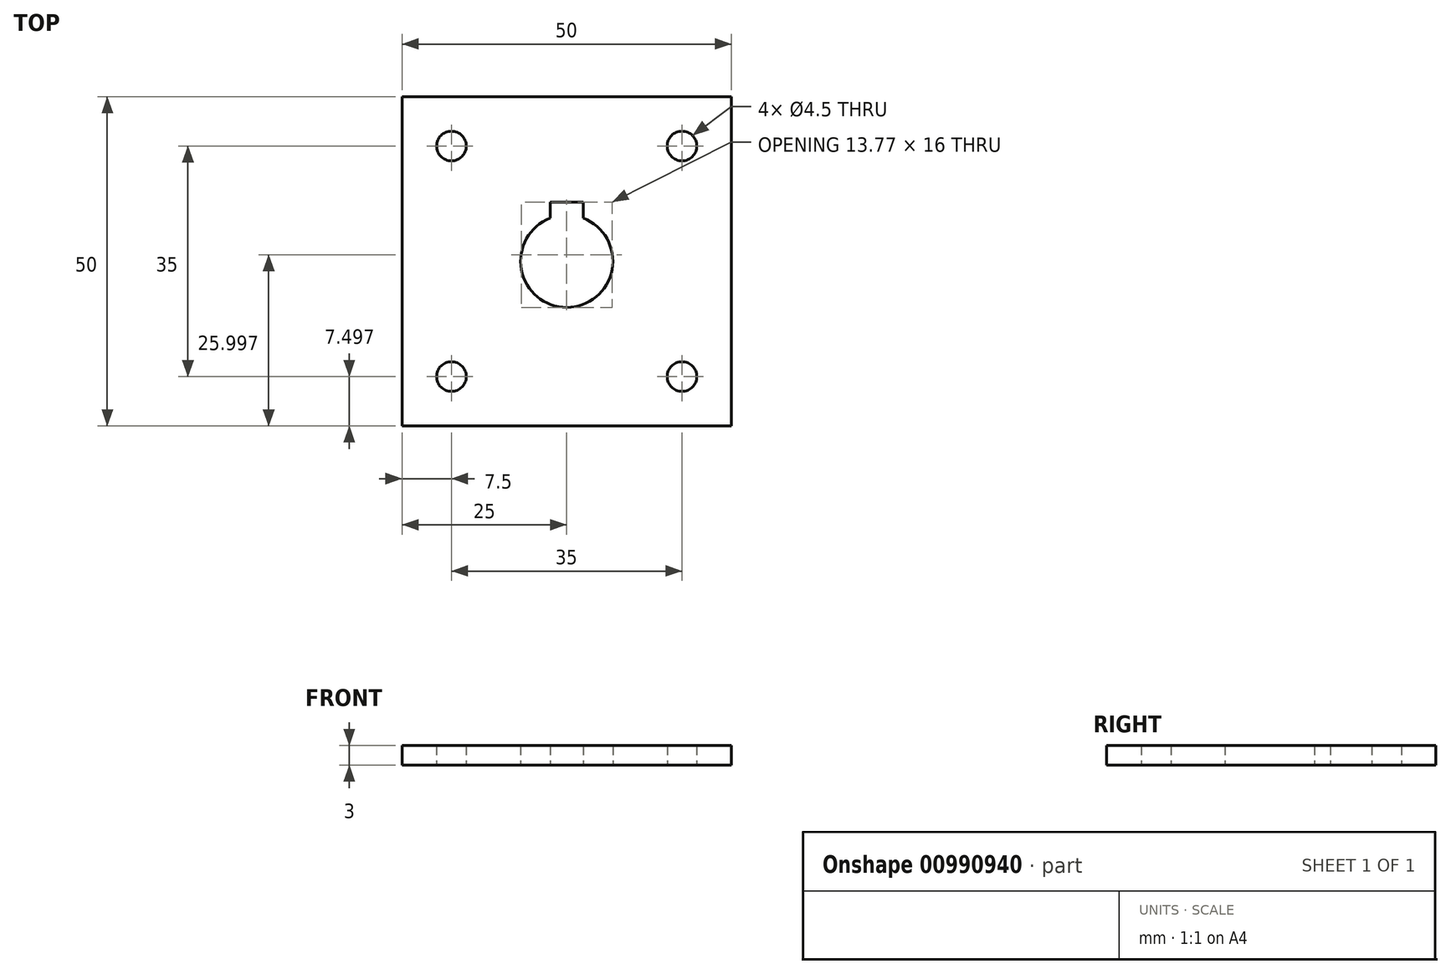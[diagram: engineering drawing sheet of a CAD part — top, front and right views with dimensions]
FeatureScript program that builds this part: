
annotation { "Feature Type Name" : "Feature", "Feature Type Description" : "" }
export const myFeature = defineFeature(function(context is Context, id is Id, definition is map)
    precondition{}
    {
        {
            var Q0;
            Q0=qCreatedBy(makeId("Top.planeOp"),FACE);
            var sketch = newSketch(context, id + "F0", { "sketchPlane" : qUnion([Q0])});
            skLineSegment(sketch, "E0.bottom", {"start": v(-75, -24.97) * mm, "end": v(-25, -24.97) * mm});
            skLineSegment(sketch, "E0.top", {"start": v(-75, -74.97) * mm, "end": v(-25, -74.97) * mm});
            skLineSegment(sketch, "E0.left", {"start": v(-75, -24.97) * mm, "end": v(-75, -74.97) * mm});
            skLineSegment(sketch, "E0.right", {"start": v(-25, -24.97) * mm, "end": v(-25, -74.97) * mm});
            skLineSegment(sketch, "E1", {"start": v(-25, -67.47) * mm, "end": v(-75, -67.47) * mm, "construction": true});
            skLineSegment(sketch, "E2", {"start": v(-25, -32.47) * mm, "end": v(-75, -32.47) * mm, "construction": true});
            skLineSegment(sketch, "E3", {"start": v(-32.5, -24.97) * mm, "end": v(-32.5, -74.97) * mm, "construction": true});
            skLineSegment(sketch, "E4", {"start": v(-67.5, -74.97) * mm, "end": v(-67.5, -24.97) * mm, "construction": true});
            skLineSegment(sketch, "E5", {"start": v(-50, -74.97) * mm, "end": v(-50, -24.97) * mm, "construction": true});
            skLineSegment(sketch, "E6", {"start": v(-47.5, -43.43) * mm, "end": v(-47.5, -40.97) * mm});
            skLineSegment(sketch, "E7", {"start": v(-47.5, -40.97) * mm, "end": v(-52.5, -40.97) * mm});
            skLineSegment(sketch, "E8", {"start": v(-52.5, -40.97) * mm, "end": v(-52.5, -43.43) * mm});
            skCircle(sketch, "E9", {"center": v(-32.5, -67.47) * mm, "radius": 2 * mm});
            skCircle(sketch, "E10", {"center": v(-67.5, -67.47) * mm, "radius": 2 * mm});
            skCircle(sketch, "E11", {"center": v(-32.5, -32.47) * mm, "radius": 2 * mm});
            skCircle(sketch, "E12", {"center": v(-67.5, -32.47) * mm, "radius": 2 * mm});
            skLineSegment(sketch, "E13", {"start": v(-25, -49.97) * mm, "end": v(-75, -49.97) * mm, "construction": true});
            skCircle(sketch, "E14.converted", {"center": v(-50, -49.97) * mm, "radius": 7 * mm});
            skSolve(sketch);
        }
        {
            var Q0;
            Q0=makeQuery(id+"F0.imprint","IMPRINT",FACE,{"disambiguationData":[TD([[makeQuery(id+"F0.imprint","IMPRINT",EDGE,{"derivedFrom":sQuery(id+"F0.wireOp",EDGE,"E0.bottom")}),-1.0]])]});
            var Q1;
            Q1=makeQuery(id+"F0.imprint","IMPRINT",FACE,{"disambiguationData":[TD([[makeQuery(id+"F0.imprint","IMPRINT",EDGE,{"derivedFrom":sQuery(id+"F0.wireOp",EDGE,"b2b6f342-489f-4b79-9c51-9a3396d51b60")}),-1.0]])]});
            extrude(context, id + "F1", {"entities" : qUnion([Q0, Q1]), "depth" : 3 * mm, "offsetDistance" : 25 * mm});
        }
        {
            var Q0;
            Q0=sQuery(id+"F0.wireOp",VERTEX,"E11.center");
            var Q1;
            Q1=sQuery(id+"F0.wireOp",VERTEX,"E9.center");
            var Q2;
            Q2=sQuery(id+"F0.wireOp",VERTEX,"E10.center");
            var Q3;
            Q3=sQuery(id+"F0.wireOp",VERTEX,"E12.center");
            var Q4;
            Q4=makeQuery(id+"F1.opExtrude","SWEPT_BODY",BODY,{"disambiguationData":[OSD([sQuery(id+"F0.wireOp",EDGE,"E0.bottom"),sQuery(id+"F0.wireOp",EDGE,"E0.top"),sQuery(id+"F0.wireOp",EDGE,"E0.left"),sQuery(id+"F0.wireOp",EDGE,"E0.right"),sQuery(id+"F0.wireOp",EDGE,"b2b6f342-489f-4b79-9c51-9a3396d51b60"),sQuery(id+"F0.wireOp",EDGE,"E6"),sQuery(id+"F0.wireOp",EDGE,"E7"),sQuery(id+"F0.wireOp",EDGE,"E8"),sQuery(id+"F0.wireOp",EDGE,"E9"),sQuery(id+"F0.wireOp",EDGE,"E10"),sQuery(id+"F0.wireOp",EDGE,"E11"),sQuery(id+"F0.wireOp",EDGE,"E12")])]});
            hole(context, id + "F2", {"style" : HoleStyle.SIMPLE, "endStyle" : HoleEndStyle.THROUGH, "oppositeDirection" : true, "standardTappedOrClearance" : lookupTablePath({ "fit" : "Normal", "standard" : "ISO", "size" : "M4", "type" : "Clearance" }), "standardBlindInLast" : lookupTablePath({ "fit" : "Normal", "standard" : "ISO", "engagement" : "75%", "pitch" : "0.7 mm", "size" : "M4", "type" : "Clearance & tapped" }), "holeDiameter" : 4.5 * mm, "majorDiameter" : 5 * mm, "isTappedThrough" : true, "tappedDepth" : 12 * mm, "tapClearance" : 3, "locations" : qUnion([Q0, Q1, Q2, Q3]), "scope" : qUnion([Q4])});
        }
    });
